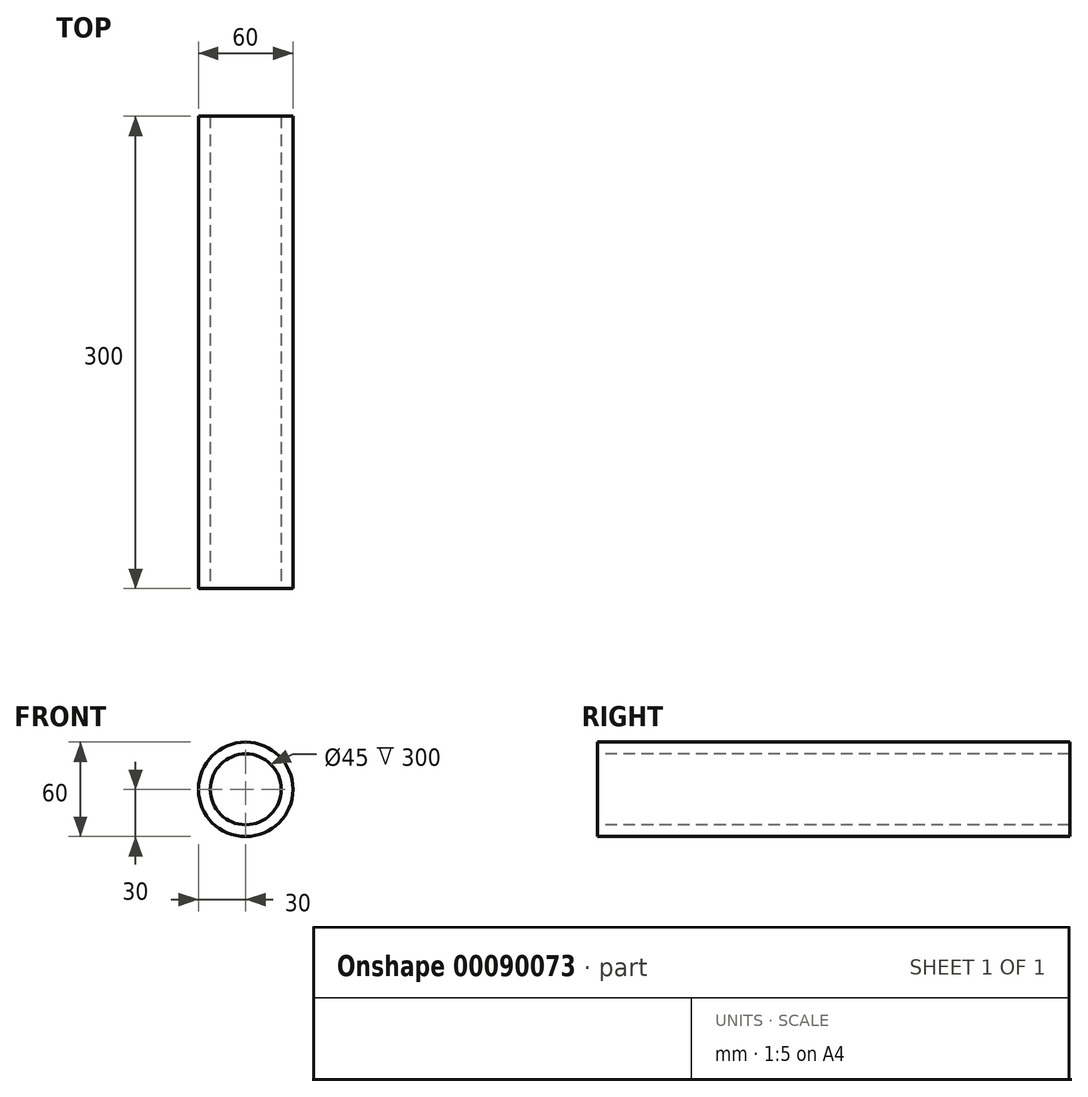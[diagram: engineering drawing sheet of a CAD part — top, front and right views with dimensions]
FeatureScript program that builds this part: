
annotation { "Feature Type Name" : "Feature", "Feature Type Description" : "" }
export const myFeature = defineFeature(function(context is Context, id is Id, definition is map)
    precondition{}
    {
        {
            var Q0;
            Q0=qCreatedBy(makeId("Front.planeOp"),FACE);
            var sketch = newSketch(context, id + "F0", { "sketchPlane" : qUnion([Q0])});
            skCircle(sketch, "E0", {"center": v(0, 0) * mm, "radius": 30 * mm});
            skCircle(sketch, "E1", {"center": v(0, 0) * mm, "radius": 22.5 * mm});
            skSolve(sketch);
        }
        {
            var Q0;
            Q0=makeQuery(id+"F0.imprint","IMPRINT",FACE,{"disambiguationData":[TD([[makeQuery(id+"F0.imprint","IMPRINT",EDGE,{"derivedFrom":sQuery(id+"F0.wireOp",EDGE,"E0")}),1.0]])]});
            extrude(context, id + "F1", {"entities" : qUnion([Q0]), "oppositeDirection" : true, "depth" : 300 * mm});
        }
    });
